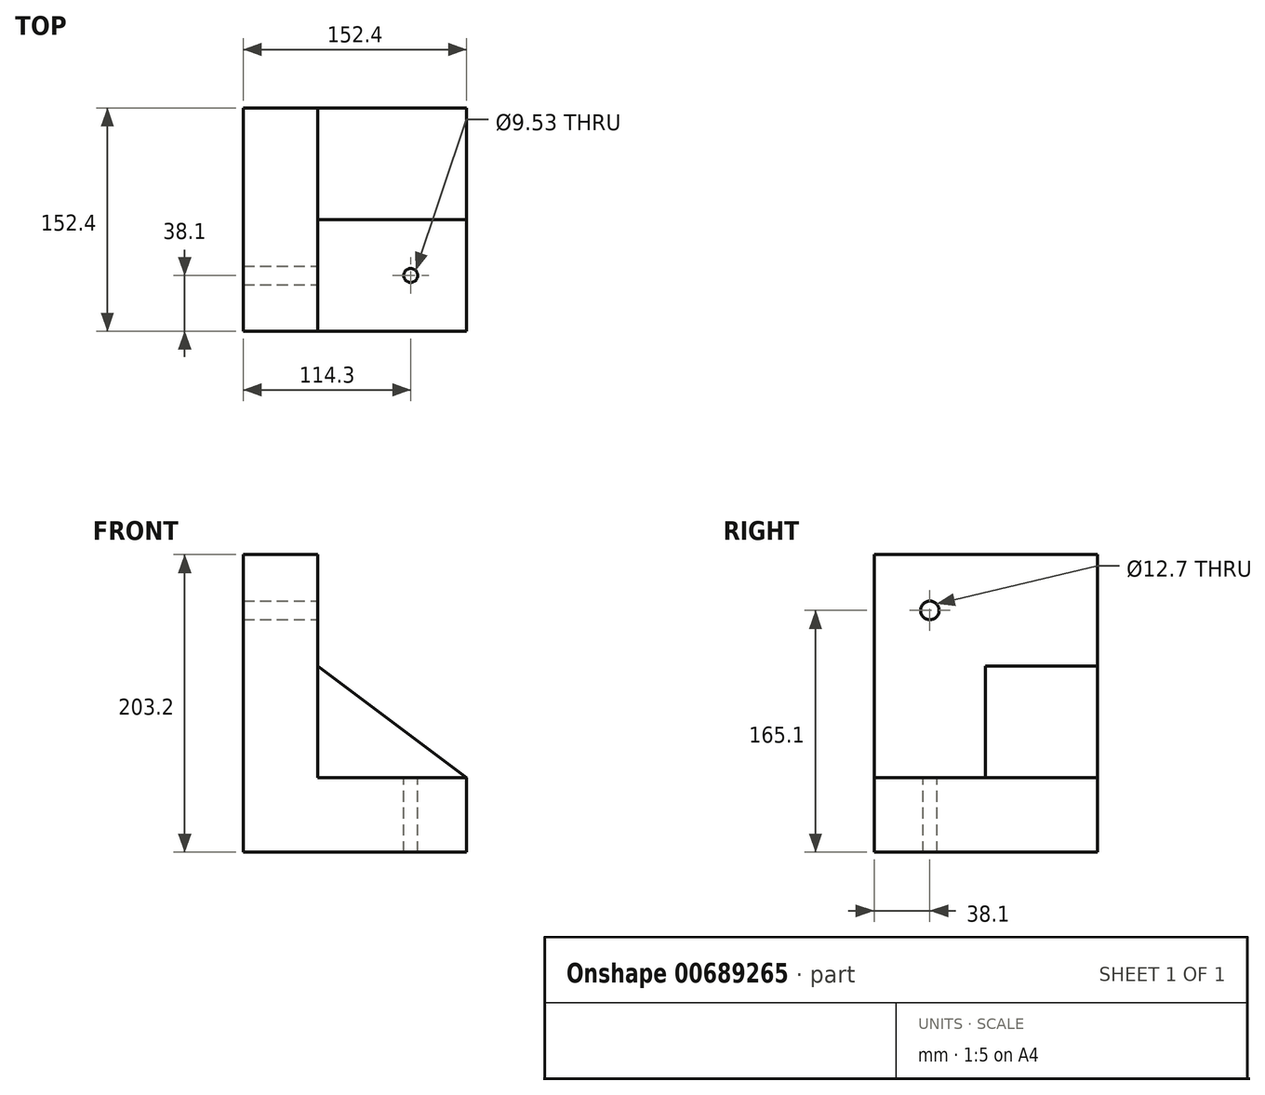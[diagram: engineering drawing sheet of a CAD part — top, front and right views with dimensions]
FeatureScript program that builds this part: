
annotation { "Feature Type Name" : "Feature", "Feature Type Description" : "" }
export const myFeature = defineFeature(function(context is Context, id is Id, definition is map)
    precondition{}
    {
        {
            var Q0;
            Q0=qCreatedBy(makeId("Front.planeOp"),FACE);
            var sketch = newSketch(context, id + "F0", { "sketchPlane" : qUnion([Q0])});
            skLineSegment(sketch, "E0", {"start": v(-50.8, 93.9) * mm, "end": v(-50.8, -109.3) * mm});
            skLineSegment(sketch, "E1", {"start": v(-50.8, -109.3) * mm, "end": v(101.6, -109.3) * mm});
            skLineSegment(sketch, "E2", {"start": v(101.6, -109.3) * mm, "end": v(101.6, -58.5) * mm});
            skLineSegment(sketch, "E3", {"start": v(101.6, -58.5) * mm, "end": v(0, -58.5) * mm});
            skLineSegment(sketch, "E4", {"start": v(0, -58.5) * mm, "end": v(0, 93.9) * mm});
            skLineSegment(sketch, "E5", {"start": v(0, 93.9) * mm, "end": v(-50.8, 93.9) * mm});
            skSolve(sketch);
        }
        {
            var Q0;
            Q0 = qSketchRegion(id + "F0", true);
            extrude(context, id + "F1", {"entities" : qUnion([Q0]), "depth" : 152.4 * mm, "offsetDistance" : 25.4 * mm});
        }
        {
            var Q0;
            Q0=makeQuery(id+"F1.opExtrude","SWEPT_FACE",FACE,{"disambiguationData":[OSD([sQuery(id+"F0.wireOp",EDGE,"E3")])]});
            var sketch = newSketch(context, id + "F2", { "sketchPlane" : qUnion([Q0])});
            skLineSegment(sketch, "E6.bottom", {"start": v(0, 0) * mm, "end": v(101.6, 0) * mm});
            skLineSegment(sketch, "E6.top", {"start": v(0, -76.2) * mm, "end": v(101.6, -76.2) * mm});
            skLineSegment(sketch, "E6.left", {"start": v(0, 0) * mm, "end": v(0, -76.2) * mm});
            skLineSegment(sketch, "E6.right", {"start": v(101.6, 0) * mm, "end": v(101.6, -76.2) * mm});
            skSolve(sketch);
        }
        {
            var Q0;
            Q0 = qSketchRegion(id + "F2", true);
            extrude(context, id + "F3", {"entities" : qUnion([Q0]), "operationType" : NewBodyOperationType.ADD, "depth" : 76.2 * mm, "offsetDistance" : 25.4 * mm});
        }
        {
            var Q0;
            Q0=makeQuery(id+"F3.opExtrude","SWEPT_FACE",FACE,{"disambiguationData":[OSD([sQuery(id+"F2.wireOp",EDGE,"E6.top")])]});
            var sketch = newSketch(context, id + "F4", { "sketchPlane" : qUnion([Q0])});
            skLineSegment(sketch, "E7", {"start": v(0, 17.7) * mm, "end": v(101.6, -58.5) * mm});
            skLineSegment(sketch, "E8", {"start": v(101.6, -58.5) * mm, "end": v(101.6, 17.7) * mm});
            skLineSegment(sketch, "E9", {"start": v(101.6, 17.7) * mm, "end": v(0, 17.7) * mm});
            skSolve(sketch);
        }
        {
            var Q0;
            Q0=makeQuery(id+"F4.imprint","IMPRINT",FACE,{"disambiguationData":[TD([[makeQuery(id+"F4.imprint","IMPRINT",EDGE,{"derivedFrom":sQuery(id+"F4.wireOp",EDGE,"E7")}),1.0]])]});
            var Q1;
            Q1=sQuery(id+"F4.wireOp",EDGE,"E9");
            var Q2;
            Q2=sQuery(id+"F4.wireOp",EDGE,"E8");
            var Q3;
            Q3=sQuery(id+"F4.wireOp",EDGE,"E7");
            extrude(context, id + "F5", {"entities" : qUnion([Q0]), "operationType" : NewBodyOperationType.REMOVE, "surfaceEntities" : qUnion([Q1, Q2, Q3]), "oppositeDirection" : true, "depth" : 76.2 * mm, "offsetDistance" : 25.4 * mm});
        }
        {
            var Q0;
            Q0=makeQuery(id+"F1.opExtrude","SWEPT_FACE",FACE,{"disambiguationData":[OSD([sQuery(id+"F0.wireOp",EDGE,"E3")])]});
            var sketch = newSketch(context, id + "F6", { "sketchPlane" : qUnion([Q0])});
            skCircle(sketch, "E10", {"center": v(63.5, -114.3) * mm, "radius": 4.76 * mm});
            skLineSegment(sketch, "E11", {"start": v(63.5, -114.3) * mm, "end": v(63.5, -119.06) * mm});
            skPoint(sketch, "E11.endSnap0", {"position": v(50.8, -152.4) * mm});
            skPoint(sketch, "E12.orphan", {"position": v(63.5, -152.4) * mm});
            skSolve(sketch);
        }
        {
            var Q0;
            Q0=sQuery(id+"F6.wireOp",VERTEX,"E10.center");
            var Q1;
            Q1=makeQuery(id+"F1.opExtrude","SWEPT_BODY",BODY,{"disambiguationData":[OSD([sQuery(id+"F0.wireOp",EDGE,"E0"),sQuery(id+"F0.wireOp",EDGE,"E1"),sQuery(id+"F0.wireOp",EDGE,"E2"),sQuery(id+"F0.wireOp",EDGE,"E3"),sQuery(id+"F0.wireOp",EDGE,"E4"),sQuery(id+"F0.wireOp",EDGE,"E5")])]});
            hole(context, id + "F7", {"style" : HoleStyle.SIMPLE, "endStyle" : HoleEndStyle.THROUGH, "holeDiameter" : 9.52 * mm, "majorDiameter" : 6.35 * mm, "isTappedThrough" : true, "tappedDepth" : 12.7 * mm, "tapClearance" : 3, "locations" : qUnion([Q0]), "scope" : qUnion([Q1])});
        }
        {
            var Q0;
            Q0=makeQuery(id+"F1.opExtrude","SWEPT_FACE",FACE,{"disambiguationData":[OSD([sQuery(id+"F0.wireOp",EDGE,"E4")])]});
            var sketch = newSketch(context, id + "F8", { "sketchPlane" : qUnion([Q0])});
            skPoint(sketch, "E13", {"position": v(-114.3, 55.8) * mm});
            skSolve(sketch);
        }
        {
            var Q0;
            Q0=sQuery(id+"F8.wireOp",VERTEX,"E13");
            var Q1;
            Q1=makeQuery(id+"F1.opExtrude","SWEPT_BODY",BODY,{"disambiguationData":[OSD([sQuery(id+"F0.wireOp",EDGE,"E0"),sQuery(id+"F0.wireOp",EDGE,"E1"),sQuery(id+"F0.wireOp",EDGE,"E2"),sQuery(id+"F0.wireOp",EDGE,"E3"),sQuery(id+"F0.wireOp",EDGE,"E4"),sQuery(id+"F0.wireOp",EDGE,"E5")])]});
            hole(context, id + "F9", {"style" : HoleStyle.SIMPLE, "endStyle" : HoleEndStyle.THROUGH, "holeDiameter" : 12.7 * mm, "majorDiameter" : 6.35 * mm, "isTappedThrough" : true, "tappedDepth" : 12.7 * mm, "tapClearance" : 3, "locations" : qUnion([Q0]), "scope" : qUnion([Q1])});
        }
    });
